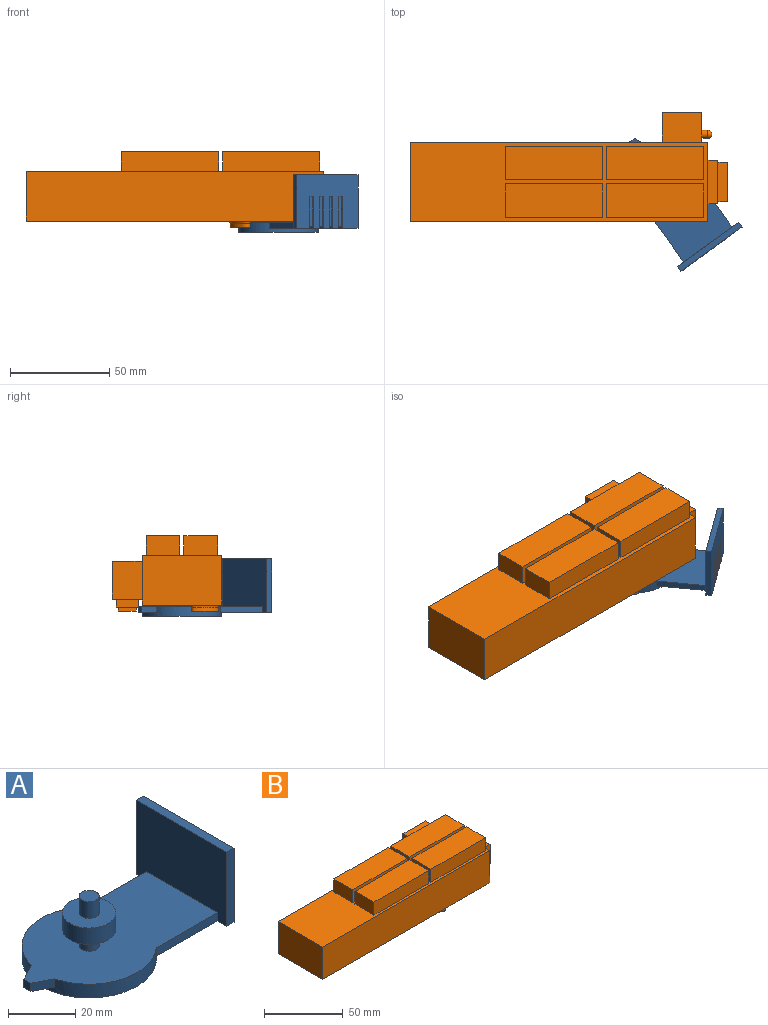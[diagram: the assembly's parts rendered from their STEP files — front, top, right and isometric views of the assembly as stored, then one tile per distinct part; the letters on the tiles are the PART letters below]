
ASSEMBLY  parts=2 mates=1
PART A: 45 faces, bbox 68x40x29 mm
  f0: plane 38x27mm, normal (1,0,0), area 871.1mm2, adj f14,f15,f17,f18,f20,f21,f23,f24
  f1: cylinder r=20mm len=40mm, axis (0,0,1), area 496.6mm2, adj f8,f9,f11,f12,f13,f29,f30,f31
  f2: plane 6x6mm, normal (0,0,1), area 28.3mm2, adj f7
  f3: cylinder r=3mm len=6mm, axis (0,0,1), area 113.1mm2, adj f4,f9
  f4: plane 16x16mm, normal (0,0,-1), area 172.8mm2, adj f3,f5
  f5: cylinder r=8mm len=16mm, axis (0,0,1), area 301.6mm2, adj f4,f6
  f6: plane 16x16mm, normal (0,0,1), area 172.8mm2, adj f5,f7
  f7: cylinder r=3mm len=6mm, axis (0,0,1), area 113.1mm2, adj f2,f6
  f8: plane 40x40mm, normal (0,0,-1), area 1256.6mm2, adj f1
  f9: plane 65x40mm, normal (0,0,1), area 1899.2mm2, adj f1,f3,f10,f11,f12,f28,f29,f30
  f10: plane 3x3mm, normal (-1,0,0), area 9mm2, adj f9,f11,f12,f13
  f11: plane 6.62x3.44mm, normal (-0.46,0.89,0), area 22.4mm2, adj f1,f9,f10,f13
  f12: plane 6.62x3.44mm, normal (-0.46,-0.89,0), area 22.4mm2, adj f1,f9,f10,f13
  f13: plane 9.87x6.62mm, normal (0,0,-1), area 38.5mm2, adj f1,f10,f11,f12
  f14: plane 27x3mm, normal (0,1,0), area 81mm2, adj f0,f28,f31,f36
  f15: plane 21x16mm, normal (0,-1,0), area 36mm2, adj f0,f16,f31,f35,f41,f42
  f16: plane 2.42x1mm, normal (1,0,0), area 2.4mm2, adj f15,f17,f31,f35
  f17: plane 21x16mm, normal (0,1,0), area 36mm2, adj f0,f16,f31,f35,f41,f42
  f18: plane 21x16mm, normal (0,-1,0), area 36mm2, adj f0,f19,f31,f34,f39,f40
  f19: plane 2.42x1mm, normal (1,0,0), area 2.4mm2, adj f18,f20,f31,f34
  f20: plane 21x16mm, normal (0,1,0), area 36mm2, adj f0,f19,f31,f34,f39,f40
  f21: plane 21x16mm, normal (0,-1,0), area 36mm2, adj f0,f22,f31,f33,f37,f38
  f22: plane 2.42x1mm, normal (1,0,0), area 2.4mm2, adj f21,f23,f31,f33
  f23: plane 21x16mm, normal (0,1,0), area 36mm2, adj f0,f22,f31,f33,f37,f38
  f24: plane 21x16mm, normal (0,-1,0), area 36mm2, adj f0,f25,f31,f32,f43,f44
  f25: plane 2.42x1mm, normal (1,0,0), area 2.4mm2, adj f24,f26,f31,f32
  f26: plane 21x16mm, normal (0,1,0), area 36mm2, adj f0,f25,f31,f32,f43,f44
  f27: plane 27x3mm, normal (0,-1,0), area 81mm2, adj f0,f28,f31,f36
  f28: plane 38x27mm, normal (-1,0,0), area 936mm2, adj f9,f14,f27,f29,f30,f31,f36
  f29: plane 25.77x3mm, normal (0,-1,0), area 77.3mm2, adj f1,f9,f28,f31
  f30: plane 25.77x3mm, normal (0,1,0), area 77.3mm2, adj f1,f9,f28,f31
  f31: plane 38x28.77mm, normal (0,0,-1), area 543mm2, adj f0,f1,f14,f15,f16,f17,f18,f19
  f32: plane 20x2.42mm, normal (0,0,-1), area 48.4mm2, adj f24,f25,f26,f43
  f33: plane 20x2.42mm, normal (0,0,-1), area 48.4mm2, adj f21,f22,f23,f37
  f34: plane 20x2.42mm, normal (0,0,-1), area 48.4mm2, adj f18,f19,f20,f39
  f35: plane 20x2.42mm, normal (0,0,-1), area 48.4mm2, adj f15,f16,f17,f41
  f36: plane 38x3mm, normal (0,0,1), area 114mm2, adj f0,f14,f27,f28
  f37: plane 15x2.42mm, normal (1,0,0), area 36.3mm2, adj f21,f23,f33,f38
  f38: plane 2.42x1mm, normal (0,0,-1), area 2.4mm2, adj f0,f21,f23,f37
  f39: plane 15x2.42mm, normal (1,0,0), area 36.3mm2, adj f18,f20,f34,f40
  f40: plane 2.42x1mm, normal (0,0,-1), area 2.4mm2, adj f0,f18,f20,f39
  f41: plane 15x2.42mm, normal (1,0,0), area 36.3mm2, adj f15,f17,f35,f42
  f42: plane 2.42x1mm, normal (0,0,-1), area 2.4mm2, adj f0,f15,f17,f41
  f43: plane 15x2.42mm, normal (1,0,0), area 36.3mm2, adj f24,f26,f32,f44
  f44: plane 2.42x1mm, normal (0,0,-1), area 2.4mm2, adj f0,f24,f26,f43
PART B: 67 faces, bbox 160x55x38 mm
  f0: plane 150x40mm, normal (0,0,-1), area 5849.3mm2, adj f1,f3,f4,f5,f36,f66
  f1: plane 40x25mm, normal (1,0,0), area 586mm2, adj f0,f2,f3,f5,f26,f27,f28,f29
  f2: plane 150x40mm, normal (0,0,1), area 2668mm2, adj f1,f3,f4,f5,f6,f7,f8,f9
  f3: plane 150x25mm, normal (0,1,0), area 3370mm2, adj f0,f1,f2,f4,f42,f43,f44,f45
  f4: plane 40x25mm, normal (-1,0,0), area 1000mm2, adj f0,f2,f3,f5
  f5: plane 150x25mm, normal (0,-1,0), area 3750mm2, adj f0,f1,f2,f4
  f6: plane 17x10mm, normal (-1,0,0), area 170mm2, adj f2,f7,f9,f10
  f7: plane 49x10mm, normal (0,-1,0), area 490mm2, adj f2,f6,f8,f10
  f8: plane 17x10mm, normal (1,0,0), area 170mm2, adj f2,f7,f9,f10
  f9: plane 49x10mm, normal (0,1,0), area 490mm2, adj f2,f6,f8,f10
  f10: plane 49x17mm, normal (0,0,1), area 833mm2, adj f6,f7,f8,f9
  f11: plane 49x10mm, normal (0,-1,0), area 490mm2, adj f2,f12,f14,f15
  f12: plane 17x10mm, normal (1,0,0), area 170mm2, adj f2,f11,f13,f15
  f13: plane 49x10mm, normal (0,1,0), area 490mm2, adj f2,f12,f14,f15
  f14: plane 17x10mm, normal (-1,0,0), area 170mm2, adj f2,f11,f13,f15
  f15: plane 49x17mm, normal (0,0,1), area 833mm2, adj f11,f12,f13,f14
  f16: plane 49x10mm, normal (0,1,0), area 490mm2, adj f2,f17,f19,f20
  f17: plane 17x10mm, normal (-1,0,0), area 170mm2, adj f2,f16,f18,f20
  f18: plane 49x10mm, normal (0,-1,0), area 490mm2, adj f2,f17,f19,f20
  f19: plane 17x10mm, normal (1,0,0), area 170mm2, adj f2,f16,f18,f20
  f20: plane 49x17mm, normal (0,0,1), area 833mm2, adj f16,f17,f18,f19
  f21: plane 49x10mm, normal (0,1,0), area 490mm2, adj f2,f22,f24,f25
  f22: plane 17x10mm, normal (-1,0,0), area 170mm2, adj f2,f21,f23,f25
  f23: plane 49x10mm, normal (0,-1,0), area 490mm2, adj f2,f22,f24,f25
  f24: plane 17x10mm, normal (1,0,0), area 170mm2, adj f2,f21,f23,f25
  f25: plane 49x17mm, normal (0,0,1), area 833mm2, adj f21,f22,f23,f24
  f26: plane 17x5mm, normal (0,1,0), area 85mm2, adj f1,f27,f29,f30
  f27: plane 22x5mm, normal (0,0,1), area 110mm2, adj f1,f26,f28,f30
  f28: plane 17x5mm, normal (0,-1,0), area 85mm2, adj f1,f27,f29,f30
  f29: plane 22x5mm, normal (0,0,-1), area 110mm2, adj f1,f26,f28,f30
  f30: plane 22x17mm, normal (1,0,0), area 74mm2, adj f26,f27,f28,f29,f32,f33,f34,f35
  f31: plane 20x15mm, normal (1,0,0), area 300mm2, adj f32,f33,f34,f35
  f32: plane 20x5mm, normal (0,0,-1), area 100mm2, adj f30,f31,f33,f35
  f33: plane 15x5mm, normal (0,-1,0), area 75mm2, adj f30,f31,f32,f34
  f34: plane 20x5mm, normal (0,0,1), area 100mm2, adj f30,f31,f33,f35
  f35: plane 15x5mm, normal (0,1,0), area 75mm2, adj f30,f31,f32,f34
  f36: cylinder r=4mm len=8mm, axis (0,0,-1), area 99.7mm2, adj f0,f37
  f37: plane 20x20mm, normal (0,0,1), area 263.9mm2, adj f36,f38
  f38: cylinder r=10mm len=20mm, axis (0,0,-1), area 502.7mm2, adj f37,f39
  f39: plane 20x20mm, normal (0,0,-1), area 263.9mm2, adj f38,f40
  f40: cylinder r=4mm len=8mm, axis (0,0,-1), area 150.8mm2, adj f39,f41
  f41: plane 8x8mm, normal (0,0,-1), area 50.3mm2, adj f40
  f42: plane 20x15mm, normal (0,0,1), area 300mm2, adj f3,f43,f45,f46
  f43: plane 19x15mm, normal (1,0,0), area 272.4mm2, adj f3,f42,f44,f46,f57
  f44: plane 20x15mm, normal (0,0,-1), area 213.5mm2, adj f3,f43,f45,f46,f47,f48,f49,f50
  f45: plane 19x15mm, normal (-1,0,0), area 285mm2, adj f3,f42,f44,f46
  f46: plane 20x19mm, normal (0,1,0), area 380mm2, adj f42,f43,f44,f45
  f47: plane 7.86x4mm, normal (0,1,0), area 31.4mm2, adj f44,f48,f50,f51
  f48: plane 11x4mm, normal (1,0,0), area 44mm2, adj f44,f47,f49,f51
  f49: plane 7.86x4mm, normal (0,-1,0), area 31.4mm2, adj f44,f48,f50,f51
  f50: plane 11x4mm, normal (-1,0,0), area 44mm2, adj f44,f47,f49,f51
  f51: plane 11x7.86mm, normal (0,0,-1), area 33.7mm2, adj f47,f48,f49,f50,f52,f53,f54,f55
  f52: plane 9x2mm, normal (1,0,0), area 18mm2, adj f51,f53,f55,f56
  f53: plane 5.86x2mm, normal (0,1,0), area 11.7mm2, adj f51,f52,f54,f56
  f54: plane 9x2mm, normal (-1,0,0), area 18mm2, adj f51,f53,f55,f56
  f55: plane 5.86x2mm, normal (0,-1,0), area 11.7mm2, adj f51,f52,f54,f56
  f56: plane 9x5.86mm, normal (0,0,-1), area 52.8mm2, adj f52,f53,f54,f55
  f57: cylinder r=2mm len=4mm, axis (-1,0,0), area 37.7mm2, adj f43,f58
  f58: sphere r=2mm, area 25.1mm2, adj f57
  f59: plane 120x10mm, normal (0,1,0), area 1200mm2, adj f1,f60,f62,f63
  f60: plane 120x4mm, normal (0,0,1), area 480mm2, adj f1,f59,f61,f63
  f61: plane 120x10mm, normal (0,-1,0), area 1200mm2, adj f1,f60,f62,f63
  f62: plane 120x4mm, normal (0,0,-1), area 480mm2, adj f1,f59,f61,f63
  f63: plane 10x4mm, normal (1,0,0), area 40mm2, adj f59,f60,f61,f62
  f64: extruded ~13.36x9.85mm, area 70.8mm2, adj f65,f66
  f65: plane 13.88x10.4mm, normal (0,0,-1), area 61.7mm2, adj f64
  f66: bspline ~15.37x11.88mm, area 59.3mm2, adj f0,f64
PLACE A rot(axis=(0,0,-1),53.9deg) t=(21.44,42.05,0.31)mm
PLACE B at identity fixed
MATE revolute A.f1 <-> B.f36  axis (0,0,1) through (52.08,0,-7.73)mm
